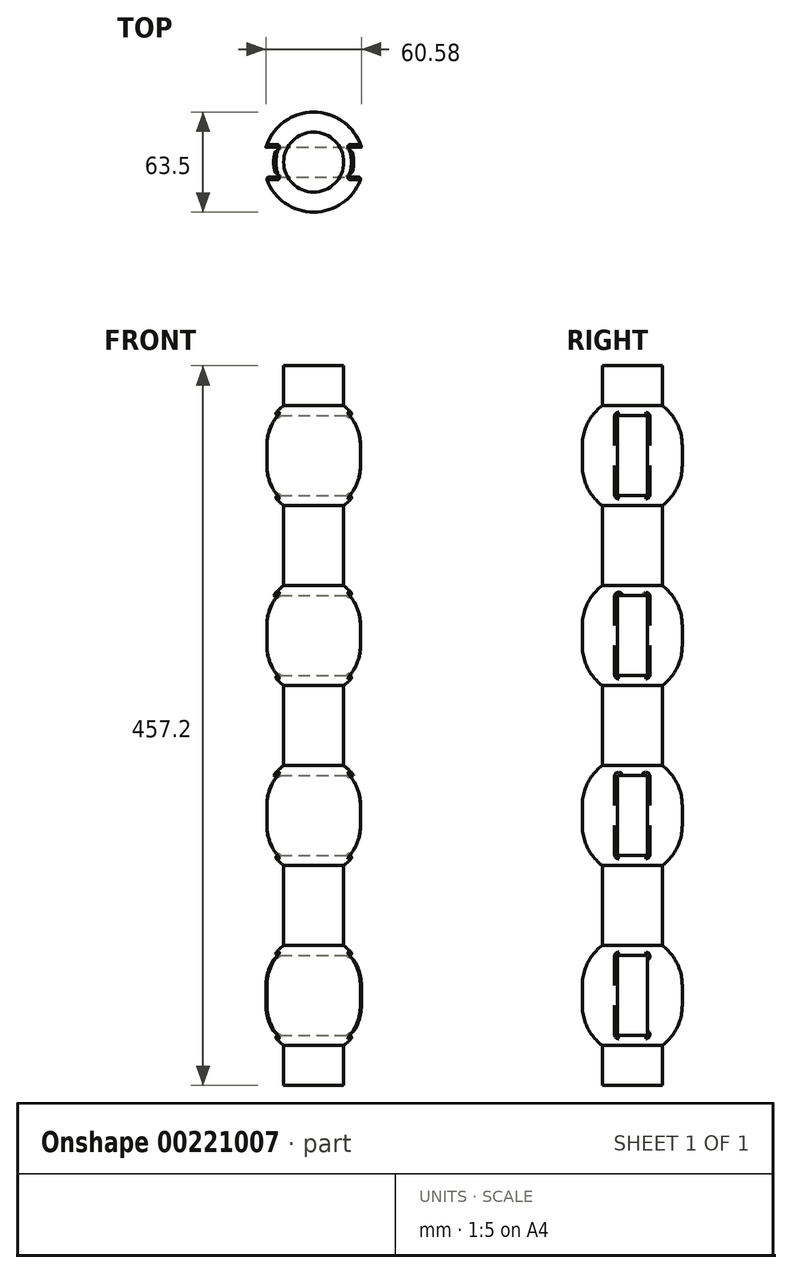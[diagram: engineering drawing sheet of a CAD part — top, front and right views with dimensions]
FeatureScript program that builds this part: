
annotation { "Feature Type Name" : "Feature", "Feature Type Description" : "" }
export const myFeature = defineFeature(function(context is Context, id is Id, definition is map)
    precondition{}
    {
        {
            var Q0;
            Q0=qCreatedBy(makeId("Top.planeOp"),FACE);
            var sketch = newSketch(context, id + "F0", { "sketchPlane" : qUnion([Q0])});
            skCircle(sketch, "E0", {"center": v(0, 0) * mm, "radius": 19.05 * mm});
            skSolve(sketch);
        }
        {
            var Q0;
            Q0 = qSketchRegion(id + "F0", true);
            extrude(context, id + "F1", {"entities" : qUnion([Q0]), "endBound" : BoundingType.SYMMETRIC, "depth" : 457.2 * mm});
        }
        {
            var Q0;
            Q0=qCreatedBy(makeId("Top.planeOp"),FACE);
            cPlane(context, id + "F2", {"entities" : qUnion([Q0]), "cplaneType" : CPlaneType.OFFSET, "offset" : 57.15 * mm, "width" : 152.4 * mm, "height" : 152.4 * mm});
        }
        {
            var Q0;
            Q0=qCreatedBy(makeId("Top.planeOp"),FACE);
            cPlane(context, id + "F3", {"entities" : qUnion([Q0]), "cplaneType" : CPlaneType.OFFSET, "offset" : 57.15 * mm, "oppositeDirection" : true, "width" : 152.4 * mm, "height" : 152.4 * mm});
        }
        {
            var Q0;
            Q0=qCreatedBy(makeId("Top.planeOp"),FACE);
            cPlane(context, id + "F4", {"entities" : qUnion([Q0]), "cplaneType" : CPlaneType.OFFSET, "offset" : 171.45 * mm, "width" : 152.4 * mm, "height" : 152.4 * mm});
        }
        {
            var Q0;
            Q0=qCreatedBy(makeId("Top.planeOp"),FACE);
            cPlane(context, id + "F5", {"entities" : qUnion([Q0]), "cplaneType" : CPlaneType.OFFSET, "offset" : 171.45 * mm, "oppositeDirection" : true, "width" : 152.4 * mm, "height" : 152.4 * mm});
        }
        {
            var Q0;
            Q0=qCreatedBy(id+"F4.planeOp",FACE);
            var sketch = newSketch(context, id + "F6", { "sketchPlane" : qUnion([Q0])});
            skCircle(sketch, "E1", {"center": v(0, 0) * mm, "radius": 31.75 * mm});
            skSolve(sketch);
        }
        {
            var Q0;
            Q0=qCreatedBy(id+"F2.planeOp",FACE);
            var sketch = newSketch(context, id + "F7", { "sketchPlane" : qUnion([Q0])});
            skCircle(sketch, "E2", {"center": v(0, 0) * mm, "radius": 31.75 * mm});
            skSolve(sketch);
        }
        {
            var Q0;
            Q0=qCreatedBy(id+"F3.planeOp",FACE);
            var sketch = newSketch(context, id + "F8", { "sketchPlane" : qUnion([Q0])});
            skCircle(sketch, "E3", {"center": v(0, 0) * mm, "radius": 31.75 * mm});
            skSolve(sketch);
        }
        {
            var Q0;
            Q0=qCreatedBy(id+"F5.planeOp",FACE);
            var sketch = newSketch(context, id + "F9", { "sketchPlane" : qUnion([Q0])});
            skCircle(sketch, "E4", {"center": v(0, 0) * mm, "radius": 31.75 * mm});
            skSolve(sketch);
        }
        {
            var Q0;
            Q0=makeQuery(id+"F6.imprint","IMPRINT",FACE,{"disambiguationData":[TD([[makeQuery(id+"F6.imprint","IMPRINT",EDGE,{"derivedFrom":sQuery(id+"F6.wireOp",EDGE,"E1")}),1.0]])]});
            var Q1;
            Q1=makeQuery(id+"F7.imprint","IMPRINT",FACE,{"disambiguationData":[TD([[makeQuery(id+"F7.imprint","IMPRINT",EDGE,{"derivedFrom":sQuery(id+"F7.wireOp",EDGE,"E2")}),1.0]])]});
            var Q2;
            Q2=makeQuery(id+"F8.imprint","IMPRINT",FACE,{"disambiguationData":[TD([[makeQuery(id+"F8.imprint","IMPRINT",EDGE,{"derivedFrom":sQuery(id+"F8.wireOp",EDGE,"E3")}),1.0]])]});
            var Q3;
            Q3=makeQuery(id+"F9.imprint","IMPRINT",FACE,{"disambiguationData":[TD([[makeQuery(id+"F9.imprint","IMPRINT",EDGE,{"derivedFrom":sQuery(id+"F9.wireOp",EDGE,"E4")}),1.0]])]});
            var Q4;
            Q4=sQuery(id+"F6.wireOp",EDGE,"E1");
            var Q5;
            Q5=sQuery(id+"F7.wireOp",EDGE,"E2");
            var Q6;
            Q6=sQuery(id+"F8.wireOp",EDGE,"E3");
            var Q7;
            Q7=sQuery(id+"F9.wireOp",EDGE,"E4");
            extrude(context, id + "F10", {"entities" : qUnion([Q0, Q1, Q2, Q3]), "operationType" : NewBodyOperationType.ADD, "surfaceEntities" : qUnion([Q4, Q5, Q6, Q7]), "endBound" : BoundingType.SYMMETRIC, "depth" : 63.5 * mm});
        }
        {
            var Q0;
            Q0=makeQuery(id+"F10.opExtrude","CAP_EDGE",EDGE,{"disambiguationData":[OSD([sQuery(id+"F6.wireOp",EDGE,"E1")])],"isStart":false});
            var Q1;
            Q1=makeQuery(id+"F10.opExtrude","CAP_EDGE",EDGE,{"disambiguationData":[OSD([sQuery(id+"F6.wireOp",EDGE,"E1")])],"isStart":true});
            var Q2;
            Q2=makeQuery(id+"F10.opExtrude","CAP_EDGE",EDGE,{"disambiguationData":[OSD([sQuery(id+"F7.wireOp",EDGE,"E2")])],"isStart":false});
            var Q3;
            Q3=makeQuery(id+"F10.opExtrude","CAP_EDGE",EDGE,{"disambiguationData":[OSD([sQuery(id+"F7.wireOp",EDGE,"E2")])],"isStart":true});
            var Q4;
            Q4=makeQuery(id+"F10.opExtrude","CAP_EDGE",EDGE,{"disambiguationData":[OSD([sQuery(id+"F8.wireOp",EDGE,"E3")])],"isStart":false});
            var Q5;
            Q5=makeQuery(id+"F10.opExtrude","CAP_EDGE",EDGE,{"disambiguationData":[OSD([sQuery(id+"F8.wireOp",EDGE,"E3")])],"isStart":true});
            var Q6;
            Q6=makeQuery(id+"F10.opExtrude","CAP_EDGE",EDGE,{"disambiguationData":[OSD([sQuery(id+"F9.wireOp",EDGE,"E4")])],"isStart":false});
            var Q7;
            Q7=makeQuery(id+"F10.opExtrude","CAP_EDGE",EDGE,{"disambiguationData":[OSD([sQuery(id+"F9.wireOp",EDGE,"E4")])],"isStart":true});
            fillet(context, id + "F11", {"entities" : qUnion([Q0, Q1, Q2, Q3, Q4, Q5, Q6, Q7]), "radius" : 31.72 * mm, "tangentPropagation" : true, "allowEdgeOverflow" : false});
        }
        {
            var Q0;
            Q0=qCreatedBy(makeId("Right.planeOp"),FACE);
            var sketch = newSketch(context, id + "F12", { "sketchPlane" : qUnion([Q0])});
            skLineSegment(sketch, "E5.bottom", {"start": v(19.05, 228.6) * mm, "end": v(-19.05, 228.6) * mm});
            skLineSegment(sketch, "E5.top", {"start": v(19.05, -228.6) * mm, "end": v(-19.05, -228.6) * mm});
            skLineSegment(sketch, "E5.left", {"start": v(19.05, 228.6) * mm, "end": v(19.05, -228.6) * mm});
            skLineSegment(sketch, "E5.right", {"start": v(-19.05, 228.6) * mm, "end": v(-19.05, -228.6) * mm});
            skPoint(sketch, "E5.middle", {"position": v(0, 0) * mm});
            skLineSegment(sketch, "E6", {"start": v(0, -228.6) * mm, "end": v(0, 228.6) * mm});
            skLineSegment(sketch, "E7.bottom", {"start": v(-9.53, 146.05) * mm, "end": v(9.52, 146.05) * mm});
            skLineSegment(sketch, "E7.top", {"start": v(-9.53, 196.85) * mm, "end": v(9.52, 196.85) * mm});
            skLineSegment(sketch, "E7.left", {"start": v(-9.53, 146.05) * mm, "end": v(-9.53, 196.85) * mm});
            skLineSegment(sketch, "E7.right", {"start": v(9.52, 146.05) * mm, "end": v(9.52, 196.85) * mm});
            skPoint(sketch, "E7.middle", {"position": v(0, 171.45) * mm});
            skLineSegment(sketch, "E8.bottom", {"start": v(-9.52, 31.75) * mm, "end": v(9.53, 31.75) * mm});
            skLineSegment(sketch, "E8.top", {"start": v(-9.52, 82.55) * mm, "end": v(9.53, 82.55) * mm});
            skLineSegment(sketch, "E8.left", {"start": v(-9.52, 31.75) * mm, "end": v(-9.52, 82.55) * mm});
            skLineSegment(sketch, "E8.right", {"start": v(9.53, 31.75) * mm, "end": v(9.53, 82.55) * mm});
            skPoint(sketch, "E8.middle", {"position": v(0, 57.15) * mm});
            skLineSegment(sketch, "E9.bottom", {"start": v(-9.53, -82.55) * mm, "end": v(9.52, -82.55) * mm});
            skLineSegment(sketch, "E9.top", {"start": v(-9.53, -31.75) * mm, "end": v(9.52, -31.75) * mm});
            skLineSegment(sketch, "E9.left", {"start": v(-9.53, -82.55) * mm, "end": v(-9.53, -31.75) * mm});
            skLineSegment(sketch, "E9.right", {"start": v(9.52, -82.55) * mm, "end": v(9.52, -31.75) * mm});
            skPoint(sketch, "E9.middle", {"position": v(0, -57.15) * mm});
            skLineSegment(sketch, "E10.bottom", {"start": v(-9.52, -196.85) * mm, "end": v(9.53, -196.85) * mm});
            skLineSegment(sketch, "E10.top", {"start": v(-9.52, -146.05) * mm, "end": v(9.53, -146.05) * mm});
            skLineSegment(sketch, "E10.left", {"start": v(-9.52, -196.85) * mm, "end": v(-9.52, -146.05) * mm});
            skLineSegment(sketch, "E10.right", {"start": v(9.53, -196.85) * mm, "end": v(9.53, -146.05) * mm});
            skPoint(sketch, "E10.middle", {"position": v(0, -171.45) * mm});
            skSolve(sketch);
        }
        {
            var Q0;
            {var subQ5=sQuery(id+"F12.wireOp",EDGE,"E10.left");Q0=makeQuery(id+"F12.imprint","IMPRINT",FACE,{"disambiguationData":[TD([[makeQuery(id+"F12.imprint","IMPRINT",EDGE,{"derivedFrom":subQ5}),-1.0]])]});}
            var Q1;
            {var subQ5=sQuery(id+"F12.wireOp",EDGE,"E10.right");Q1=makeQuery(id+"F12.imprint","IMPRINT",FACE,{"disambiguationData":[TD([[makeQuery(id+"F12.imprint","IMPRINT",EDGE,{"derivedFrom":subQ5}),1.0]])]});}
            var Q2;
            {var subQ5=sQuery(id+"F12.wireOp",EDGE,"E9.left");Q2=makeQuery(id+"F12.imprint","IMPRINT",FACE,{"disambiguationData":[TD([[makeQuery(id+"F12.imprint","IMPRINT",EDGE,{"derivedFrom":subQ5}),-1.0]])]});}
            var Q3;
            {var subQ5=sQuery(id+"F12.wireOp",EDGE,"E9.right");Q3=makeQuery(id+"F12.imprint","IMPRINT",FACE,{"disambiguationData":[TD([[makeQuery(id+"F12.imprint","IMPRINT",EDGE,{"derivedFrom":subQ5}),1.0]])]});}
            var Q4;
            {var subQ5=sQuery(id+"F12.wireOp",EDGE,"E8.left");Q4=makeQuery(id+"F12.imprint","IMPRINT",FACE,{"disambiguationData":[TD([[makeQuery(id+"F12.imprint","IMPRINT",EDGE,{"derivedFrom":subQ5}),-1.0]])]});}
            var Q5;
            {var subQ5=sQuery(id+"F12.wireOp",EDGE,"E8.right");Q5=makeQuery(id+"F12.imprint","IMPRINT",FACE,{"disambiguationData":[TD([[makeQuery(id+"F12.imprint","IMPRINT",EDGE,{"derivedFrom":subQ5}),1.0]])]});}
            var Q6;
            {var subQ5=sQuery(id+"F12.wireOp",EDGE,"E7.left");Q6=makeQuery(id+"F12.imprint","IMPRINT",FACE,{"disambiguationData":[TD([[makeQuery(id+"F12.imprint","IMPRINT",EDGE,{"derivedFrom":subQ5}),-1.0]])]});}
            var Q7;
            {var subQ5=sQuery(id+"F12.wireOp",EDGE,"E7.right");Q7=makeQuery(id+"F12.imprint","IMPRINT",FACE,{"disambiguationData":[TD([[makeQuery(id+"F12.imprint","IMPRINT",EDGE,{"derivedFrom":subQ5}),1.0]])]});}
            extrude(context, id + "F13", {"entities" : qUnion([Q0, Q1, Q2, Q3, Q4, Q5, Q6, Q7]), "operationType" : NewBodyOperationType.REMOVE, "endBound" : BoundingType.SYMMETRIC, "oppositeDirection" : true, "depth" : 63.5 * mm});
        }
        {
            var Q0;
            {var subQ0=sQuery(id+"F6.wireOp",EDGE,"E1");Q0=makeQuery(id+"F13.boolean.opBoolean","INTERSECT",EDGE,{"disambiguationData":[OD(1.0)],"derivedFrom":[makeQuery(id+"F11.opFillet","BLEND_FACE",FACE,{"disambiguationData":[OSD([subQ0]),TDD([makeQuery(id+"F10.opExtrude","CAP_EDGE",EDGE,{"disambiguationData":[OSD([subQ0])],"isStart":true})])]}),makeQuery(id+"F13.opExtrude","SWEPT_FACE",FACE,{"disambiguationData":[OSD([sQuery(id+"F12.wireOp",EDGE,"E7.left")])]})]});}
            var Q1;
            Q1=makeQuery(id+"F13.boolean.opBoolean","INTERSECT",EDGE,{"disambiguationData":[OD(1.0)],"derivedFrom":[makeQuery(id+"F10.opExtrude","SWEPT_FACE",FACE,{"disambiguationData":[OSD([sQuery(id+"F6.wireOp",EDGE,"E1")])]}),makeQuery(id+"F13.opExtrude","SWEPT_FACE",FACE,{"disambiguationData":[OSD([sQuery(id+"F12.wireOp",EDGE,"E7.left")])]})]});
            var Q2;
            {var subQ0=sQuery(id+"F6.wireOp",EDGE,"E1");Q2=makeQuery(id+"F13.boolean.opBoolean","INTERSECT",EDGE,{"disambiguationData":[OD(1.0)],"derivedFrom":[makeQuery(id+"F11.opFillet","BLEND_FACE",FACE,{"disambiguationData":[OSD([subQ0]),TDD([makeQuery(id+"F10.opExtrude","CAP_EDGE",EDGE,{"disambiguationData":[OSD([subQ0])],"isStart":false})])]}),makeQuery(id+"F13.opExtrude","SWEPT_FACE",FACE,{"disambiguationData":[OSD([sQuery(id+"F12.wireOp",EDGE,"E7.left")])]})]});}
            var Q3;
            {var subQ0=sQuery(id+"F6.wireOp",EDGE,"E1");Q3=makeQuery(id+"F13.boolean.opBoolean","INTERSECT",EDGE,{"disambiguationData":[OD(1.0)],"derivedFrom":[makeQuery(id+"F11.opFillet","BLEND_FACE",FACE,{"disambiguationData":[OSD([subQ0]),TDD([makeQuery(id+"F10.opExtrude","CAP_EDGE",EDGE,{"disambiguationData":[OSD([subQ0])],"isStart":false})])]}),makeQuery(id+"F13.opExtrude","SWEPT_FACE",FACE,{"disambiguationData":[OSD([sQuery(id+"F12.wireOp",EDGE,"E7.top")])]})]});}
            var Q4;
            {var subQ0=sQuery(id+"F6.wireOp",EDGE,"E1");Q4=makeQuery(id+"F13.boolean.opBoolean","INTERSECT",EDGE,{"disambiguationData":[OD(0.0)],"derivedFrom":[makeQuery(id+"F11.opFillet","BLEND_FACE",FACE,{"disambiguationData":[OSD([subQ0]),TDD([makeQuery(id+"F10.opExtrude","CAP_EDGE",EDGE,{"disambiguationData":[OSD([subQ0])],"isStart":false})])]}),makeQuery(id+"F13.opExtrude","SWEPT_FACE",FACE,{"disambiguationData":[OSD([sQuery(id+"F12.wireOp",EDGE,"E7.top")])]})]});}
            var Q5;
            {var subQ0=sQuery(id+"F6.wireOp",EDGE,"E1");Q5=makeQuery(id+"F13.boolean.opBoolean","INTERSECT",EDGE,{"disambiguationData":[OD(0.0)],"derivedFrom":[makeQuery(id+"F11.opFillet","BLEND_FACE",FACE,{"disambiguationData":[OSD([subQ0]),TDD([makeQuery(id+"F10.opExtrude","CAP_EDGE",EDGE,{"disambiguationData":[OSD([subQ0])],"isStart":false})])]}),makeQuery(id+"F13.opExtrude","SWEPT_FACE",FACE,{"disambiguationData":[OSD([sQuery(id+"F12.wireOp",EDGE,"E7.left")])]})]});}
            var Q6;
            Q6=makeQuery(id+"F13.boolean.opBoolean","INTERSECT",EDGE,{"disambiguationData":[OD(0.0)],"derivedFrom":[makeQuery(id+"F10.opExtrude","SWEPT_FACE",FACE,{"disambiguationData":[OSD([sQuery(id+"F6.wireOp",EDGE,"E1")])]}),makeQuery(id+"F13.opExtrude","SWEPT_FACE",FACE,{"disambiguationData":[OSD([sQuery(id+"F12.wireOp",EDGE,"E7.left")])]})]});
            var Q7;
            {var subQ0=sQuery(id+"F6.wireOp",EDGE,"E1");Q7=makeQuery(id+"F13.boolean.opBoolean","INTERSECT",EDGE,{"disambiguationData":[OD(0.0)],"derivedFrom":[makeQuery(id+"F11.opFillet","BLEND_FACE",FACE,{"disambiguationData":[OSD([subQ0]),TDD([makeQuery(id+"F10.opExtrude","CAP_EDGE",EDGE,{"disambiguationData":[OSD([subQ0])],"isStart":true})])]}),makeQuery(id+"F13.opExtrude","SWEPT_FACE",FACE,{"disambiguationData":[OSD([sQuery(id+"F12.wireOp",EDGE,"E7.left")])]})]});}
            var Q8;
            {var subQ0=sQuery(id+"F6.wireOp",EDGE,"E1");Q8=makeQuery(id+"F13.boolean.opBoolean","INTERSECT",EDGE,{"disambiguationData":[OD(1.0)],"derivedFrom":[makeQuery(id+"F11.opFillet","BLEND_FACE",FACE,{"disambiguationData":[OSD([subQ0]),TDD([makeQuery(id+"F10.opExtrude","CAP_EDGE",EDGE,{"disambiguationData":[OSD([subQ0])],"isStart":true})])]}),makeQuery(id+"F13.opExtrude","SWEPT_FACE",FACE,{"disambiguationData":[OSD([sQuery(id+"F12.wireOp",EDGE,"E7.bottom")])]})]});}
            var Q9;
            {var subQ0=sQuery(id+"F6.wireOp",EDGE,"E1");Q9=makeQuery(id+"F13.boolean.opBoolean","INTERSECT",EDGE,{"disambiguationData":[OD(1.0)],"derivedFrom":[makeQuery(id+"F11.opFillet","BLEND_FACE",FACE,{"disambiguationData":[OSD([subQ0]),TDD([makeQuery(id+"F10.opExtrude","CAP_EDGE",EDGE,{"disambiguationData":[OSD([subQ0])],"isStart":true})])]}),makeQuery(id+"F13.opExtrude","SWEPT_FACE",FACE,{"disambiguationData":[OSD([sQuery(id+"F12.wireOp",EDGE,"E7.right")])]})]});}
            var Q10;
            Q10=makeQuery(id+"F13.boolean.opBoolean","INTERSECT",EDGE,{"disambiguationData":[OD(1.0)],"derivedFrom":[makeQuery(id+"F10.opExtrude","SWEPT_FACE",FACE,{"disambiguationData":[OSD([sQuery(id+"F6.wireOp",EDGE,"E1")])]}),makeQuery(id+"F13.opExtrude","SWEPT_FACE",FACE,{"disambiguationData":[OSD([sQuery(id+"F12.wireOp",EDGE,"E7.right")])]})]});
            var Q11;
            {var subQ0=sQuery(id+"F6.wireOp",EDGE,"E1");Q11=makeQuery(id+"F13.boolean.opBoolean","INTERSECT",EDGE,{"disambiguationData":[OD(1.0)],"derivedFrom":[makeQuery(id+"F11.opFillet","BLEND_FACE",FACE,{"disambiguationData":[OSD([subQ0]),TDD([makeQuery(id+"F10.opExtrude","CAP_EDGE",EDGE,{"disambiguationData":[OSD([subQ0])],"isStart":false})])]}),makeQuery(id+"F13.opExtrude","SWEPT_FACE",FACE,{"disambiguationData":[OSD([sQuery(id+"F12.wireOp",EDGE,"E7.right")])]})]});}
            var Q12;
            {var subQ0=sQuery(id+"F6.wireOp",EDGE,"E1");Q12=makeQuery(id+"F13.boolean.opBoolean","INTERSECT",EDGE,{"disambiguationData":[OD(0.0)],"derivedFrom":[makeQuery(id+"F11.opFillet","BLEND_FACE",FACE,{"disambiguationData":[OSD([subQ0]),TDD([makeQuery(id+"F10.opExtrude","CAP_EDGE",EDGE,{"disambiguationData":[OSD([subQ0])],"isStart":false})])]}),makeQuery(id+"F13.opExtrude","SWEPT_FACE",FACE,{"disambiguationData":[OSD([sQuery(id+"F12.wireOp",EDGE,"E7.right")])]})]});}
            var Q13;
            Q13=makeQuery(id+"F13.boolean.opBoolean","INTERSECT",EDGE,{"disambiguationData":[OD(0.0)],"derivedFrom":[makeQuery(id+"F10.opExtrude","SWEPT_FACE",FACE,{"disambiguationData":[OSD([sQuery(id+"F6.wireOp",EDGE,"E1")])]}),makeQuery(id+"F13.opExtrude","SWEPT_FACE",FACE,{"disambiguationData":[OSD([sQuery(id+"F12.wireOp",EDGE,"E7.right")])]})]});
            var Q14;
            {var subQ0=sQuery(id+"F6.wireOp",EDGE,"E1");Q14=makeQuery(id+"F13.boolean.opBoolean","INTERSECT",EDGE,{"disambiguationData":[OD(0.0)],"derivedFrom":[makeQuery(id+"F11.opFillet","BLEND_FACE",FACE,{"disambiguationData":[OSD([subQ0]),TDD([makeQuery(id+"F10.opExtrude","CAP_EDGE",EDGE,{"disambiguationData":[OSD([subQ0])],"isStart":true})])]}),makeQuery(id+"F13.opExtrude","SWEPT_FACE",FACE,{"disambiguationData":[OSD([sQuery(id+"F12.wireOp",EDGE,"E7.right")])]})]});}
            var Q15;
            {var subQ0=sQuery(id+"F6.wireOp",EDGE,"E1");Q15=makeQuery(id+"F13.boolean.opBoolean","INTERSECT",EDGE,{"disambiguationData":[OD(0.0)],"derivedFrom":[makeQuery(id+"F11.opFillet","BLEND_FACE",FACE,{"disambiguationData":[OSD([subQ0]),TDD([makeQuery(id+"F10.opExtrude","CAP_EDGE",EDGE,{"disambiguationData":[OSD([subQ0])],"isStart":true})])]}),makeQuery(id+"F13.opExtrude","SWEPT_FACE",FACE,{"disambiguationData":[OSD([sQuery(id+"F12.wireOp",EDGE,"E7.bottom")])]})]});}
            var Q16;
            {var subQ0=sQuery(id+"F7.wireOp",EDGE,"E2");Q16=makeQuery(id+"F13.boolean.opBoolean","INTERSECT",EDGE,{"disambiguationData":[OD(1.0)],"derivedFrom":[makeQuery(id+"F11.opFillet","BLEND_FACE",FACE,{"disambiguationData":[OSD([subQ0]),TDD([makeQuery(id+"F10.opExtrude","CAP_EDGE",EDGE,{"disambiguationData":[OSD([subQ0])],"isStart":false})])]}),makeQuery(id+"F13.opExtrude","SWEPT_FACE",FACE,{"disambiguationData":[OSD([sQuery(id+"F12.wireOp",EDGE,"E8.top")])]})]});}
            var Q17;
            {var subQ0=sQuery(id+"F7.wireOp",EDGE,"E2");Q17=makeQuery(id+"F13.boolean.opBoolean","INTERSECT",EDGE,{"disambiguationData":[OD(1.0)],"derivedFrom":[makeQuery(id+"F11.opFillet","BLEND_FACE",FACE,{"disambiguationData":[OSD([subQ0]),TDD([makeQuery(id+"F10.opExtrude","CAP_EDGE",EDGE,{"disambiguationData":[OSD([subQ0])],"isStart":true})])]}),makeQuery(id+"F13.opExtrude","SWEPT_FACE",FACE,{"disambiguationData":[OSD([sQuery(id+"F12.wireOp",EDGE,"E8.bottom")])]})]});}
            var Q18;
            {var subQ0=sQuery(id+"F7.wireOp",EDGE,"E2");Q18=makeQuery(id+"F13.boolean.opBoolean","INTERSECT",EDGE,{"disambiguationData":[OD(0.0)],"derivedFrom":[makeQuery(id+"F11.opFillet","BLEND_FACE",FACE,{"disambiguationData":[OSD([subQ0]),TDD([makeQuery(id+"F10.opExtrude","CAP_EDGE",EDGE,{"disambiguationData":[OSD([subQ0])],"isStart":true})])]}),makeQuery(id+"F13.opExtrude","SWEPT_FACE",FACE,{"disambiguationData":[OSD([sQuery(id+"F12.wireOp",EDGE,"E8.bottom")])]})]});}
            var Q19;
            Q19=makeQuery(id+"F13.boolean.opBoolean","COPY",FACE,{"derivedFrom":makeQuery(id+"F13.opExtrude","SWEPT_FACE",FACE,{"disambiguationData":[OSD([sQuery(id+"F12.wireOp",EDGE,"E8.right")])]})});
            var Q20;
            Q20=makeQuery(id+"F13.boolean.opBoolean","COPY",FACE,{"derivedFrom":makeQuery(id+"F13.opExtrude","SWEPT_FACE",FACE,{"disambiguationData":[OSD([sQuery(id+"F12.wireOp",EDGE,"E8.left")])]})});
            var Q21;
            Q21=makeQuery(id+"F13.boolean.opBoolean","COPY",FACE,{"derivedFrom":makeQuery(id+"F13.opExtrude","SWEPT_FACE",FACE,{"disambiguationData":[OSD([sQuery(id+"F12.wireOp",EDGE,"E7.right")])]})});
            var Q22;
            Q22=makeQuery(id+"F13.boolean.opBoolean","COPY",FACE,{"derivedFrom":makeQuery(id+"F13.opExtrude","SWEPT_FACE",FACE,{"disambiguationData":[OSD([sQuery(id+"F12.wireOp",EDGE,"E7.left")])]})});
            var Q23;
            Q23=makeQuery(id+"F13.boolean.opBoolean","COPY",FACE,{"derivedFrom":makeQuery(id+"F13.opExtrude","SWEPT_FACE",FACE,{"disambiguationData":[OSD([sQuery(id+"F12.wireOp",EDGE,"E9.right")])]})});
            var Q24;
            Q24=makeQuery(id+"F13.boolean.opBoolean","COPY",FACE,{"derivedFrom":makeQuery(id+"F13.opExtrude","SWEPT_FACE",FACE,{"disambiguationData":[OSD([sQuery(id+"F12.wireOp",EDGE,"E9.bottom")])]})});
            var Q25;
            Q25=makeQuery(id+"F13.boolean.opBoolean","COPY",FACE,{"derivedFrom":makeQuery(id+"F13.opExtrude","SWEPT_FACE",FACE,{"disambiguationData":[OSD([sQuery(id+"F12.wireOp",EDGE,"E9.left")])]})});
            var Q26;
            Q26=makeQuery(id+"F13.boolean.opBoolean","COPY",FACE,{"derivedFrom":makeQuery(id+"F13.opExtrude","SWEPT_FACE",FACE,{"disambiguationData":[OSD([sQuery(id+"F12.wireOp",EDGE,"E10.top")])]})});
            var Q27;
            Q27=makeQuery(id+"F13.boolean.opBoolean","COPY",FACE,{"derivedFrom":makeQuery(id+"F13.opExtrude","SWEPT_FACE",FACE,{"disambiguationData":[OSD([sQuery(id+"F12.wireOp",EDGE,"E10.left")])]})});
            var Q28;
            Q28=makeQuery(id+"F13.boolean.opBoolean","COPY",FACE,{"derivedFrom":makeQuery(id+"F13.opExtrude","SWEPT_FACE",FACE,{"disambiguationData":[OSD([sQuery(id+"F12.wireOp",EDGE,"E10.bottom")])]})});
            fillet(context, id + "F14", {"entities" : qUnion([Q0, Q1, Q2, Q3, Q4, Q5, Q6, Q7, Q8, Q9, Q10, Q11, Q12, Q13, Q14, Q15, Q16, Q17, Q18, Q19, Q20, Q21, Q22, Q23, Q24, Q25, Q26, Q27, Q28]), "radius" : 1.27 * mm, "tangentPropagation" : true, "allowEdgeOverflow" : false});
        }
    });
